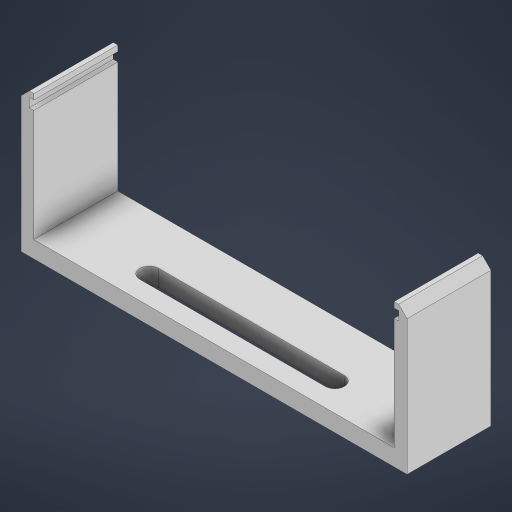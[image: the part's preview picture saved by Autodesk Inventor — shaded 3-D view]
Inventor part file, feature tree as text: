
AUTODESK INVENTOR PART (.ipt)
format: ipt  version: 2023 (Build 270158000, 158)  size: 217,600 bytes
history: native  units: mm
features: extrude x2, sketch x2, mirror x1, chamfer x1, projected_geometry x1
ambient origin geometry x8: Origin, YZ Plane, XZ Plane, XY Plane, X Axis, Y Axis, Z Axis, Center Point
bodies: Solid1 (feature_tree)
feature tree (7):
  extrude  "Extrusion1"  Depth=0.8mm
  mirror  "Mirror1"
  extrude  "Extrusion2"  Depth=1.6mm
  chamfer  "Chamfer1"  Distance=1.5mm
  sketch  "Sketch1"  dims[d0=3.0mm d2=0.8mm]
  sketch  "Sketch2"  dims[d3=1.0mm d4=1.6mm d5=1.5mm d9=20.0mm d10=15.0mm d11=0.0mm d12=1.7mm d13=0.0mm d14=0.0mm d15=66.0mm d16=1.5mm d17=2.0mm d18=45.0deg]
  projected_geometry  "Projected Loop1"
